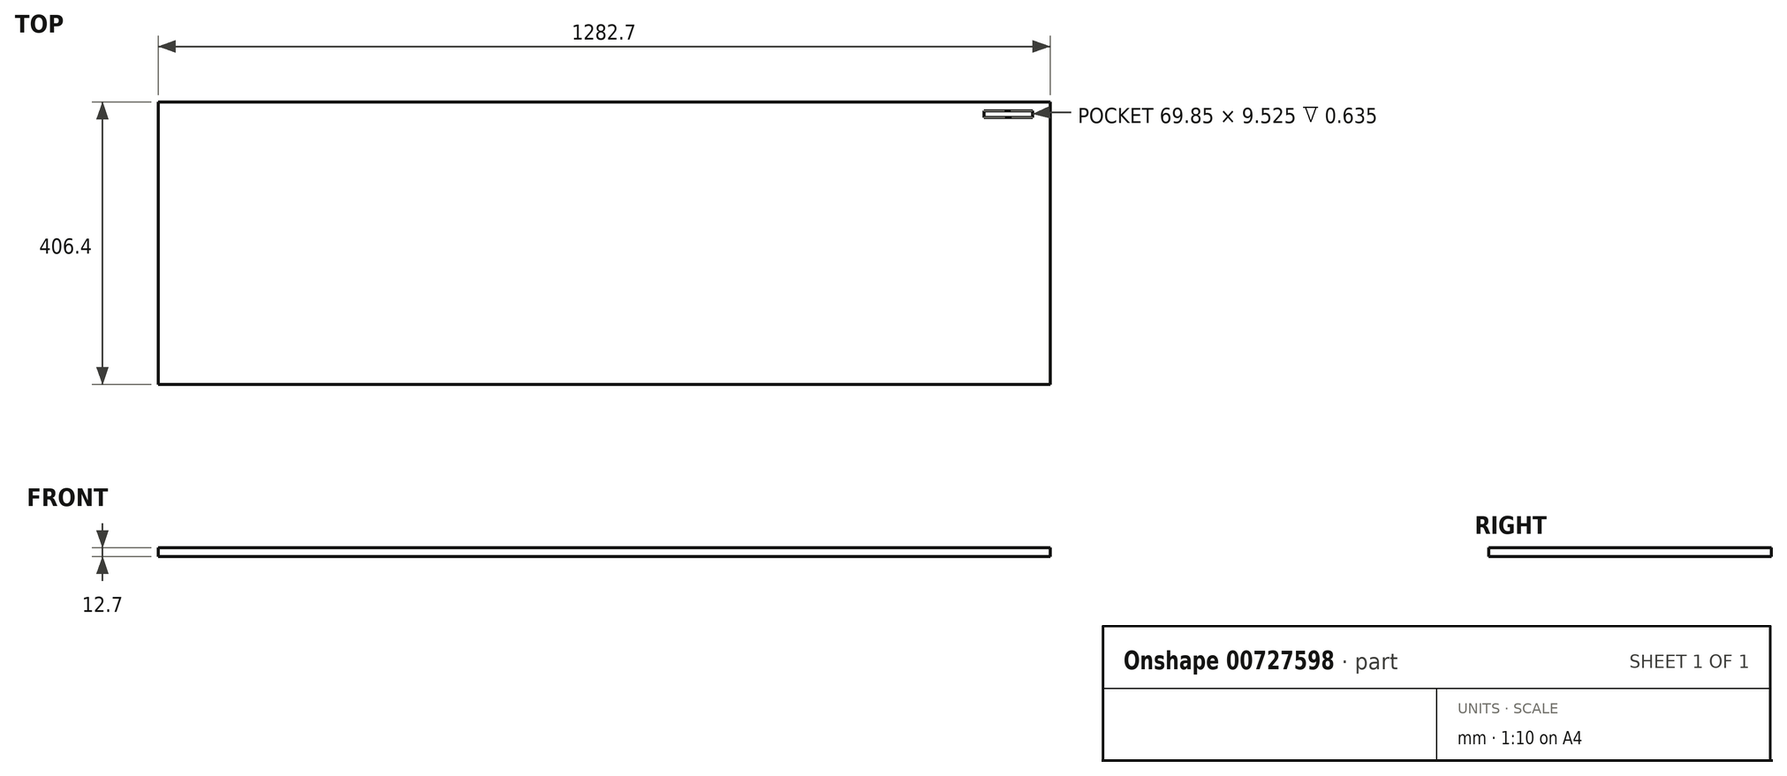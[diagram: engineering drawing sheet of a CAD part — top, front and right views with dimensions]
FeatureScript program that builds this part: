
annotation { "Feature Type Name" : "Feature", "Feature Type Description" : "" }
export const myFeature = defineFeature(function(context is Context, id is Id, definition is map)
    precondition{}
    {
        {
            var Q0;
            Q0=qCreatedBy(makeId("Top.planeOp"),FACE);
            var sketch = newSketch(context, id + "F0", { "sketchPlane" : qUnion([Q0])});
            skLineSegment(sketch, "E0.bottom", {"start": v(641.35, 203.2) * mm, "end": v(-641.35, 203.2) * mm});
            skLineSegment(sketch, "E0.top", {"start": v(641.35, -203.2) * mm, "end": v(-641.35, -203.2) * mm});
            skLineSegment(sketch, "E0.left", {"start": v(641.35, 203.2) * mm, "end": v(641.35, -203.2) * mm});
            skLineSegment(sketch, "E0.right", {"start": v(-641.35, 203.2) * mm, "end": v(-641.35, -203.2) * mm});
            skPoint(sketch, "E0.middle", {"position": v(0, 0) * mm});
            skSolve(sketch);
        }
        {
            var Q0;
            Q0 = qSketchRegion(id + "F0", true);
            extrude(context, id + "F1", {"entities" : qUnion([Q0]), "endBound" : BoundingType.SYMMETRIC, "depth" : 12.7 * mm, "offsetDistance" : 25.4 * mm});
        }
        {
            var Q0;
            Q0=makeQuery(id+"F1.opExtrude","CAP_FACE",FACE,{"disambiguationData":[OSD([sQuery(id+"F0.wireOp",EDGE,"E0.bottom"),sQuery(id+"F0.wireOp",EDGE,"E0.top"),sQuery(id+"F0.wireOp",EDGE,"E0.left"),sQuery(id+"F0.wireOp",EDGE,"E0.right")])],"isStart":false});
            var sketch = newSketch(context, id + "F2", { "sketchPlane" : qUnion([Q0])});
            skLineSegment(sketch, "E1.bottom", {"start": v(546.1, 190.5) * mm, "end": v(615.95, 190.5) * mm});
            skLineSegment(sketch, "E1.top", {"start": v(546.1, 180.97) * mm, "end": v(615.95, 180.97) * mm});
            skLineSegment(sketch, "E1.left", {"start": v(546.1, 190.5) * mm, "end": v(546.1, 180.98) * mm});
            skLineSegment(sketch, "E1.right", {"start": v(615.95, 190.5) * mm, "end": v(615.95, 180.98) * mm});
            skSolve(sketch);
        }
        {
            var Q0;
            Q0 = qSketchRegion(id + "F2", true);
            extrude(context, id + "F3", {"entities" : qUnion([Q0]), "operationType" : NewBodyOperationType.REMOVE, "oppositeDirection" : true, "depth" : 0.64 * mm, "offsetDistance" : 25.4 * mm});
        }
    });
